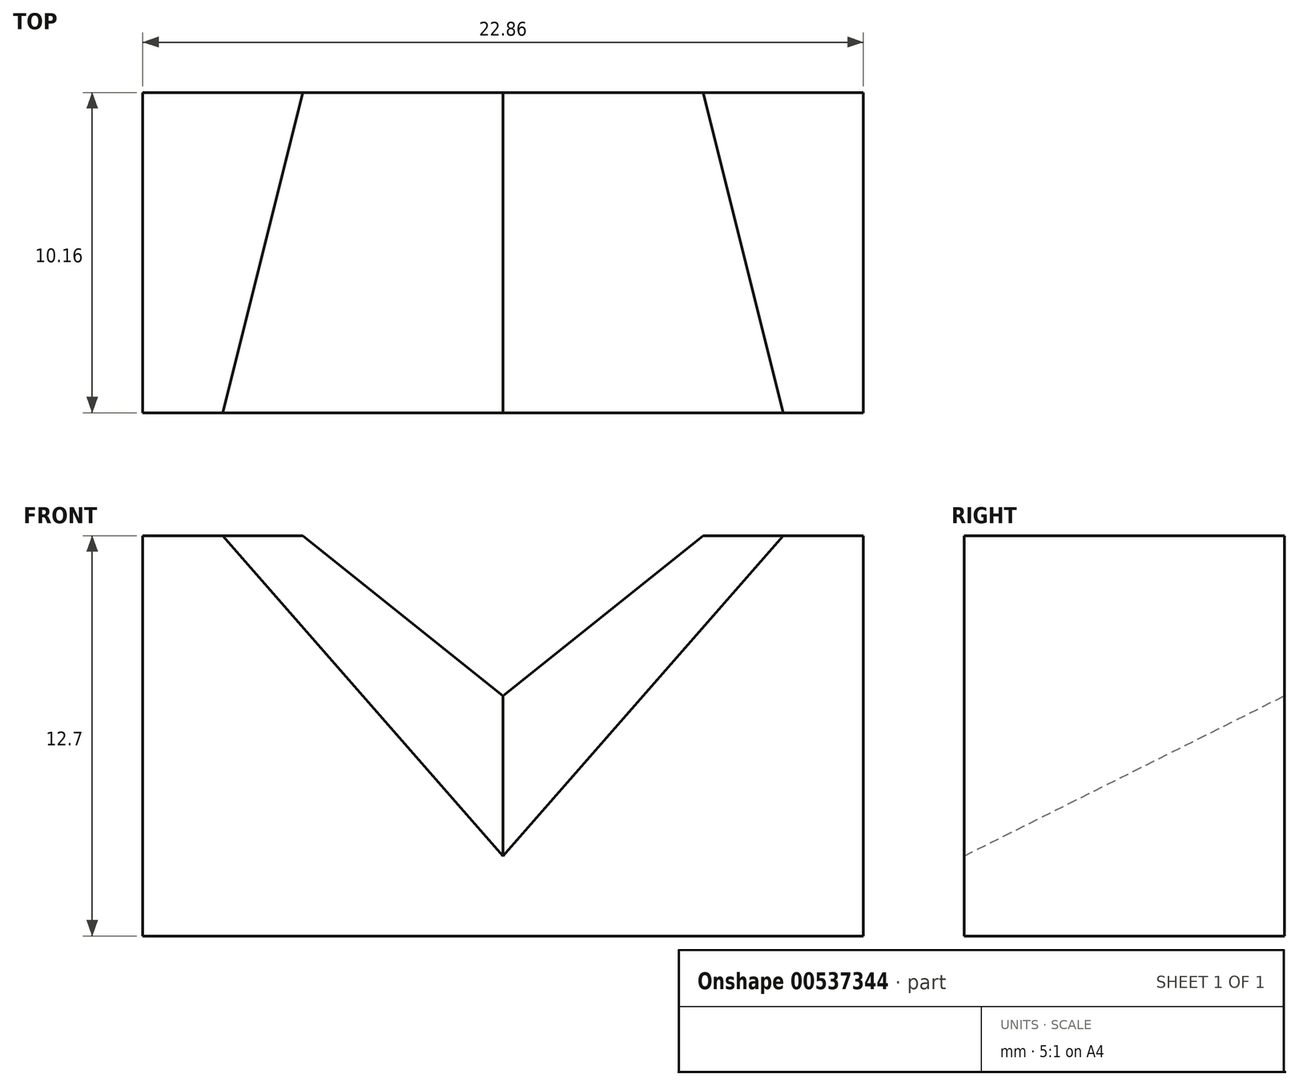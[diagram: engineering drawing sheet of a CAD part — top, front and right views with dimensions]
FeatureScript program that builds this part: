
annotation { "Feature Type Name" : "Feature", "Feature Type Description" : "" }
export const myFeature = defineFeature(function(context is Context, id is Id, definition is map)
    precondition{}
    {
        {
            var Q0;
            Q0=qCreatedBy(makeId("Front.planeOp"),FACE);
            var sketch = newSketch(context, id + "F0", { "sketchPlane" : qUnion([Q0])});
            skLineSegment(sketch, "E0", {"start": v(-39.15, 0) * mm, "end": v(-16.29, 0) * mm});
            skLineSegment(sketch, "E1", {"start": v(-39.15, 0) * mm, "end": v(-39.15, 12.7) * mm});
            skLineSegment(sketch, "E2", {"start": v(-39.15, 12.7) * mm, "end": v(-16.29, 12.7) * mm});
            skLineSegment(sketch, "E3", {"start": v(-16.29, 12.7) * mm, "end": v(-16.29, 0) * mm});
            skSolve(sketch);
        }
        {
            var Q0;
            Q0=makeQuery(id+"F0.imprint","IMPRINT",FACE,{"disambiguationData":[TD([[makeQuery(id+"F0.imprint","IMPRINT",EDGE,{"derivedFrom":sQuery(id+"F0.wireOp",EDGE,"E0")}),1.0]])]});
            extrude(context, id + "F1", {"entities" : qUnion([Q0]), "depth" : 10.16 * mm, "offsetDistance" : 25.4 * mm});
        }
        {
            var Q0;
            Q0=makeQuery(id+"F1.opExtrude","CAP_FACE",FACE,{"disambiguationData":[OSD([sQuery(id+"F0.wireOp",EDGE,"E0"),sQuery(id+"F0.wireOp",EDGE,"E1"),sQuery(id+"F0.wireOp",EDGE,"E2"),sQuery(id+"F0.wireOp",EDGE,"E3")])],"isStart":false});
            var sketch = newSketch(context, id + "F2", { "sketchPlane" : qUnion([Q0])});
            skLineSegment(sketch, "E4", {"start": v(-39.15, 0) * mm, "end": v(-27.72, 0) * mm, "construction": true});
            skLineSegment(sketch, "E5", {"start": v(-27.72, 0) * mm, "end": v(-27.72, 2.54) * mm, "construction": true});
            skLineSegment(sketch, "E6", {"start": v(-39.15, 12.7) * mm, "end": v(-36.6, 12.7) * mm});
            skLineSegment(sketch, "E7", {"start": v(-36.6, 12.7) * mm, "end": v(-27.72, 2.54) * mm});
            skLineSegment(sketch, "E8", {"start": v(-16.29, 12.7) * mm, "end": v(-18.83, 12.7) * mm});
            skLineSegment(sketch, "E9", {"start": v(-18.83, 12.7) * mm, "end": v(-27.72, 2.54) * mm});
            skSolve(sketch);
        }
        {
            var Q0;
            Q0=makeQuery(id+"F1.opExtrude","CAP_FACE",FACE,{"disambiguationData":[OSD([sQuery(id+"F0.wireOp",EDGE,"E0"),sQuery(id+"F0.wireOp",EDGE,"E1"),sQuery(id+"F0.wireOp",EDGE,"E2"),sQuery(id+"F0.wireOp",EDGE,"E3")])],"isStart":true});
            var sketch = newSketch(context, id + "F3", { "sketchPlane" : qUnion([Q0])});
            skLineSegment(sketch, "E10", {"start": v(16.29, 0) * mm, "end": v(27.72, 0) * mm, "construction": true});
            skLineSegment(sketch, "E11", {"start": v(27.72, 0) * mm, "end": v(27.72, 7.62) * mm, "construction": true});
            skLineSegment(sketch, "E12", {"start": v(16.29, 12.7) * mm, "end": v(21.37, 12.7) * mm, "construction": true});
            skLineSegment(sketch, "E13", {"start": v(39.15, 12.7) * mm, "end": v(34.07, 12.7) * mm, "construction": true});
            skLineSegment(sketch, "E14", {"start": v(21.37, 12.7) * mm, "end": v(27.72, 7.62) * mm});
            skLineSegment(sketch, "E15", {"start": v(27.72, 7.62) * mm, "end": v(34.07, 12.7) * mm});
            skSolve(sketch);
        }
        {
            var Q1;
            {var subQ0=sQuery(id+"F2.wireOp",EDGE,"E7");Q1=makeQuery(id+"F2.imprint","IMPRINT",FACE,{"disambiguationData":[TD([[makeQuery(id+"F2.imprint","IMPRINT",EDGE,{"derivedFrom":subQ0}),1.0]])]});}
            var Q2;
            {var subQ0=sQuery(id+"F3.wireOp",EDGE,"E14");Q2=makeQuery(id+"F3.imprint","IMPRINT",FACE,{"disambiguationData":[TD([[makeQuery(id+"F3.imprint","IMPRINT",EDGE,{"derivedFrom":subQ0}),1.0]])]});}
            loft(context, id + "F4", {"operationType" : NewBodyOperationType.REMOVE, "sheetProfilesArray" : [{ "sheetProfileEntities" : qUnion([Q1]) }, { "sheetProfileEntities" : qUnion([Q2]) }]});
        }
    });
